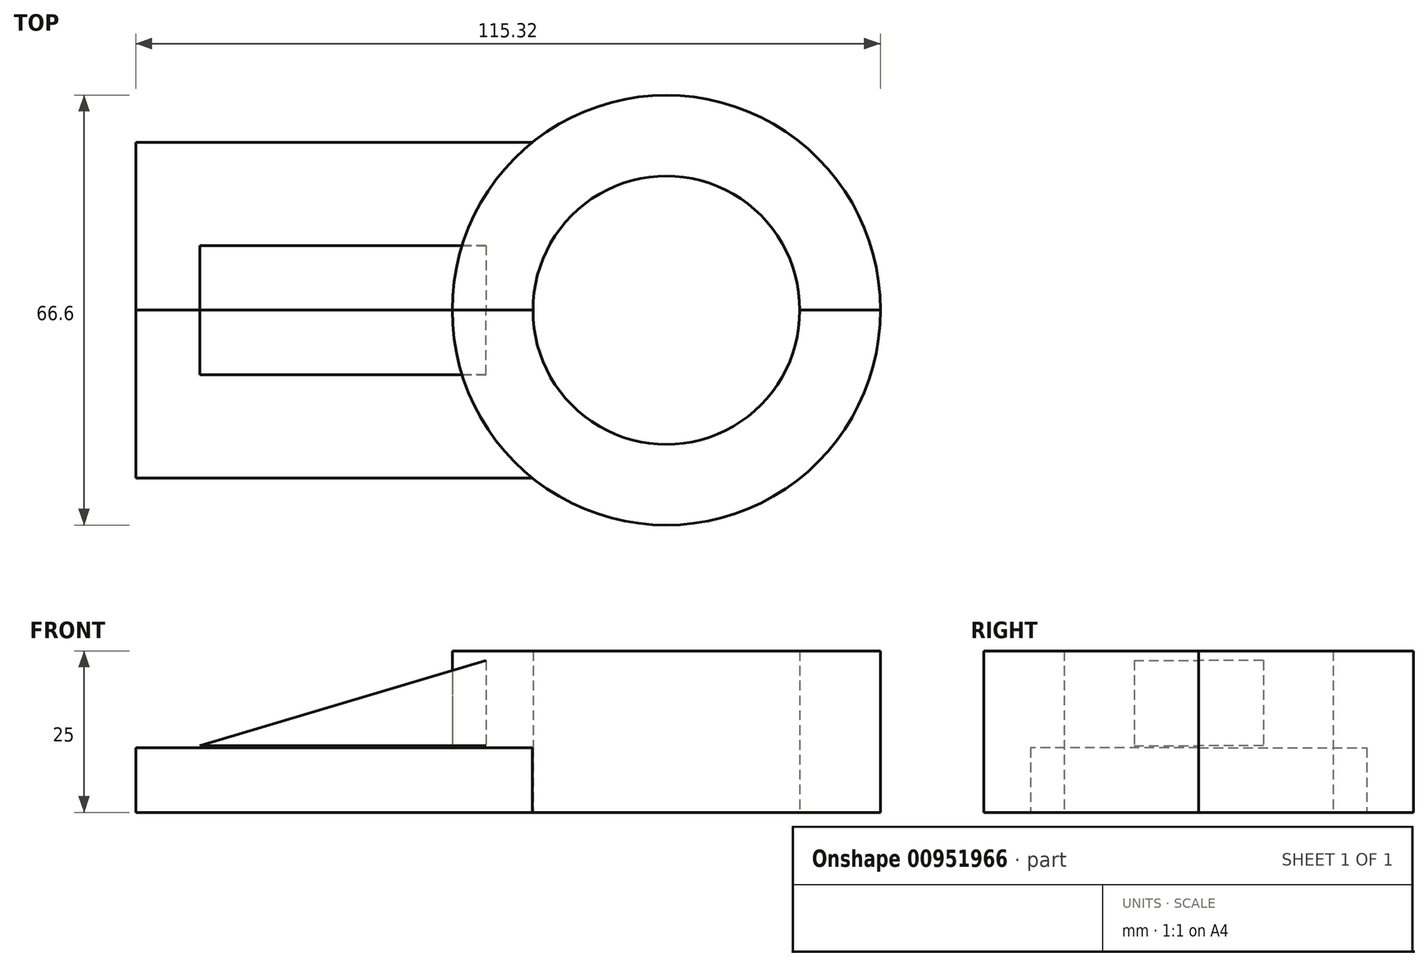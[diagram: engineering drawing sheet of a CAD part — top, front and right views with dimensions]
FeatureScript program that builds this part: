
annotation { "Feature Type Name" : "Feature", "Feature Type Description" : "" }
export const myFeature = defineFeature(function(context is Context, id is Id, definition is map)
    precondition{}
    {
        {
            var Q0;
            Q0=qCreatedBy(makeId("Top.planeOp"),FACE);
            var sketch = newSketch(context, id + "F0", { "sketchPlane" : qUnion([Q0])});
            skArc(sketch, "E0", {"start": v(-12.5, 0) * mm, "mid": v(20.64, -33.3) * mm, "end": v(53.78, 0) * mm});
            skArc(sketch, "E1", {"start": v(0, 0) * mm, "mid": v(20.64, -20.8) * mm, "end": v(41.28, 0) * mm});
            skLineSegment(sketch, "E2", {"start": v(-12.5, 0) * mm, "end": v(0, 0) * mm});
            skLineSegment(sketch, "E3", {"start": v(41.28, 0) * mm, "end": v(53.78, 0) * mm});
            skSolve(sketch);
        }
        {
            var Q0;
            Q0=makeQuery(id+"F0.imprint","IMPRINT",FACE,{"disambiguationData":[TD([[makeQuery(id+"F0.imprint","IMPRINT",EDGE,{"derivedFrom":sQuery(id+"F0.wireOp",EDGE,"E1")}),-1.0]])]});
            extrude(context, id + "F1", {"entities" : qUnion([Q0]), "depth" : 25 * mm, "offsetDistance" : 25 * mm});
        }
        {
            var Q0;
            Q0=qCreatedBy(makeId("Top.planeOp"),FACE);
            var sketch = newSketch(context, id + "F2", { "sketchPlane" : qUnion([Q0])});
            skLineSegment(sketch, "E4.bottom", {"start": v(0, 0) * mm, "end": v(-61.54, 0) * mm});
            skLineSegment(sketch, "E4.top", {"start": v(0, -26.02) * mm, "end": v(-61.54, -26.02) * mm});
            skLineSegment(sketch, "E4.left", {"start": v(0, 0) * mm, "end": v(0, -26.02) * mm});
            skLineSegment(sketch, "E4.right", {"start": v(-61.54, 0) * mm, "end": v(-61.54, -26.02) * mm});
            skSolve(sketch);
        }
        {
            var Q0;
            Q0=makeQuery(id+"F2.imprint","IMPRINT",FACE,{"disambiguationData":[TD([[makeQuery(id+"F2.imprint","IMPRINT",EDGE,{"derivedFrom":sQuery(id+"F2.wireOp",EDGE,"E4.bottom")}),1.0]])]});
            extrude(context, id + "F3", {"entities" : qUnion([Q0]), "operationType" : NewBodyOperationType.ADD, "depth" : 10 * mm, "offsetDistance" : 25 * mm});
        }
        {
            var Q0;
            Q0=qCreatedBy(makeId("Front.planeOp"),FACE);
            var sketch = newSketch(context, id + "F4", { "sketchPlane" : qUnion([Q0])});
            skLineSegment(sketch, "E5", {"start": v(-7.3, 10.33) * mm, "end": v(-51.63, 10.33) * mm});
            skLineSegment(sketch, "E6", {"start": v(-51.63, 10.33) * mm, "end": v(-7.3, 23.53) * mm});
            skLineSegment(sketch, "E7", {"start": v(-7.3, 23.53) * mm, "end": v(-7.3, 10.33) * mm});
            skSolve(sketch);
        }
        {
            var Q0;
            Q0 = qSketchRegion(id + "F4", true);
            extrude(context, id + "F5", {"entities" : qUnion([Q0]), "depth" : 10 * mm, "offsetDistance" : 25 * mm});
        }
        {
            var Q0;
            Q0=makeQuery(id+"F1.opExtrude","SWEPT_BODY",BODY,{"disambiguationData":[OSD([sQuery(id+"F0.wireOp",EDGE,"E0"),sQuery(id+"F0.wireOp",EDGE,"E1"),sQuery(id+"F0.wireOp",EDGE,"E2"),sQuery(id+"F0.wireOp",EDGE,"E3")])]});
            var Q1;
            Q1=makeQuery(id+"F5.opExtrude","SWEPT_BODY",BODY,{"disambiguationData":[OSD([sQuery(id+"F4.wireOp",EDGE,"E5"),sQuery(id+"F4.wireOp",EDGE,"E6"),sQuery(id+"F4.wireOp",EDGE,"E7")])]});
            var Q2;
            Q2=qCreatedBy(makeId("Front.planeOp"),FACE);
            mirror(context, id + "F6", {"entities" : qUnion([Q0, Q1]), "mirrorPlane" : qUnion([Q2])});
        }
    });
